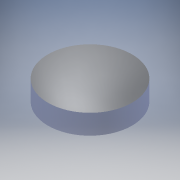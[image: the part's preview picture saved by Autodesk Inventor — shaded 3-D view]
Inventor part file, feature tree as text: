
AUTODESK INVENTOR PART (.ipt)
format: ipt  version: 2016 (Build 200138000, 138)  size: 107,008 bytes
history: native  units: mm
features: extrude x1, sketch x1
ambient origin geometry x8: Origin, YZ Plane, XZ Plane, XY Plane, X Axis, Y Axis, Z Axis, Center Point
bodies: Solid1 (feature_tree)
feature tree (2):
  extrude  "Extrusion1"  Depth=12.0mm TaperAngle=0.0deg
  sketch  "Sketch1"  dims[d0=50.8mm d1=12.0mm d2=0.0mm]
